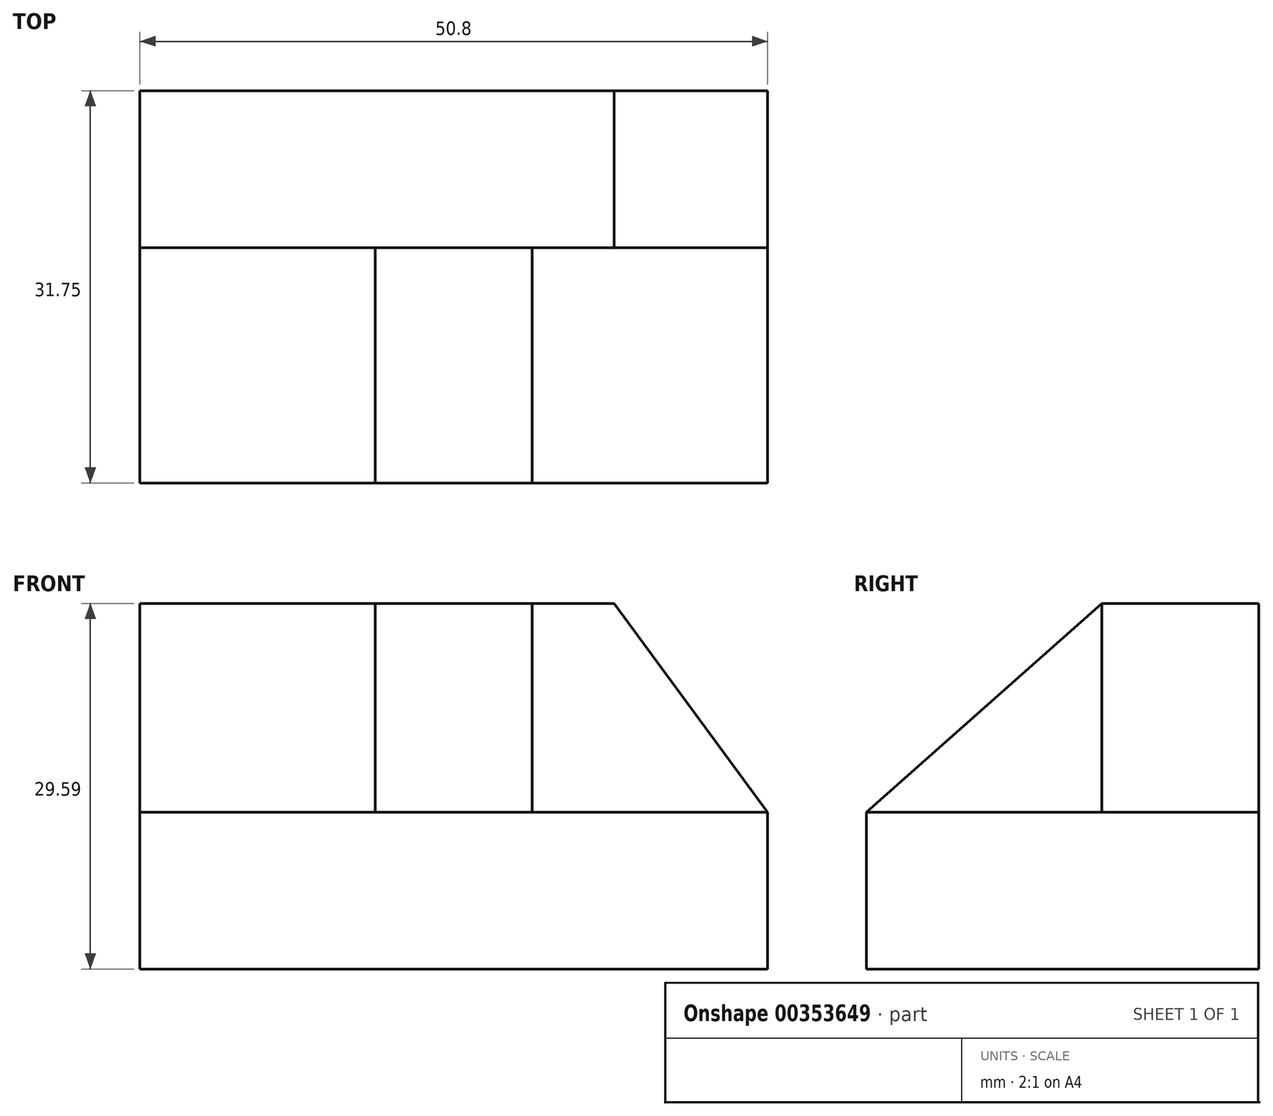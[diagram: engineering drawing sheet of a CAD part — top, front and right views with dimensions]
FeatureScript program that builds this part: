
annotation { "Feature Type Name" : "Feature", "Feature Type Description" : "" }
export const myFeature = defineFeature(function(context is Context, id is Id, definition is map)
    precondition{}
    {
        {
            var Q0;
            Q0=qCreatedBy(makeId("Right.planeOp"),FACE);
            var sketch = newSketch(context, id + "F0", { "sketchPlane" : qUnion([Q0])});
            skLineSegment(sketch, "E0", {"start": v(-31.75, 0) * mm, "end": v(-31.75, 12.7) * mm});
            skLineSegment(sketch, "E1", {"start": v(-31.75, 12.7) * mm, "end": v(-12.7, 12.7) * mm});
            skLineSegment(sketch, "E2", {"start": v(-12.7, 12.7) * mm, "end": v(-12.7, 29.59) * mm});
            skLineSegment(sketch, "E3", {"start": v(-12.7, 29.59) * mm, "end": v(0, 29.59) * mm});
            skLineSegment(sketch, "E4", {"start": v(0, 29.59) * mm, "end": v(0, 0) * mm});
            skLineSegment(sketch, "E5", {"start": v(-31.75, 0) * mm, "end": v(0, 0) * mm});
            skSolve(sketch);
        }
        {
            var Q0;
            Q0 = qSketchRegion(id + "F0", true);
            extrude(context, id + "F1", {"entities" : qUnion([Q0]), "depth" : 50.8 * mm});
        }
        {
            var Q0;
            Q0=makeQuery(id+"F1.opExtrude","SWEPT_FACE",FACE,{"disambiguationData":[OSD([sQuery(id+"F0.wireOp",EDGE,"E2")])]});
            var sketch = newSketch(context, id + "F2", { "sketchPlane" : qUnion([Q0])});
            skLineSegment(sketch, "E6", {"start": v(50.8, 12.7) * mm, "end": v(38.37, 29.59) * mm});
            skLineSegment(sketch, "E7", {"start": v(38.37, 29.59) * mm, "end": v(50.8, 29.59) * mm});
            skLineSegment(sketch, "E8", {"start": v(50.8, 29.59) * mm, "end": v(50.8, 12.7) * mm});
            skSolve(sketch);
        }
        {
            var Q0;
            Q0 = qSketchRegion(id + "F2", true);
            extrude(context, id + "F3", {"entities" : qUnion([Q0]), "operationType" : NewBodyOperationType.REMOVE, "oppositeDirection" : true, "depth" : 25.4 * mm});
        }
        {
            var Q0;
            Q0=makeQuery(id+"F1.opExtrude","SWEPT_FACE",FACE,{"disambiguationData":[OSD([sQuery(id+"F0.wireOp",EDGE,"E1")])]});
            var sketch = newSketch(context, id + "F4", { "sketchPlane" : qUnion([Q0])});
            skLineSegment(sketch, "E9", {"start": v(19.05, -12.7) * mm, "end": v(19.05, -31.75) * mm});
            skLineSegment(sketch, "E10", {"start": v(19.05, -31.75) * mm, "end": v(31.75, -31.75) * mm});
            skLineSegment(sketch, "E11", {"start": v(31.75, -31.75) * mm, "end": v(31.75, -12.7) * mm});
            skLineSegment(sketch, "E12", {"start": v(31.75, -12.7) * mm, "end": v(19.05, -12.7) * mm});
            skSolve(sketch);
        }
        {
            var Q0;
            Q0=makeQuery(id+"F4.imprint","IMPRINT",FACE,{"disambiguationData":[TD([[makeQuery(id+"F4.imprint","IMPRINT",EDGE,{"derivedFrom":sQuery(id+"F4.wireOp",EDGE,"E9")}),1.0]])]});
            extrude(context, id + "F5", {"entities" : qUnion([Q0]), "operationType" : NewBodyOperationType.ADD, "depth" : 17.02 * mm});
        }
        {
            var Q0;
            Q0=makeQuery(id+"F5.opExtrude","SWEPT_FACE",FACE,{"disambiguationData":[OSD([sQuery(id+"F4.wireOp",EDGE,"E11")])]});
            var sketch = newSketch(context, id + "F6", { "sketchPlane" : qUnion([Q0])});
            skLineSegment(sketch, "E13", {"start": v(-31.75, 12.7) * mm, "end": v(-12.7, 29.59) * mm});
            skLineSegment(sketch, "E14", {"start": v(-31.75, 12.7) * mm, "end": v(-31.75, 29.72) * mm});
            skLineSegment(sketch, "E15", {"start": v(-31.75, 29.72) * mm, "end": v(-12.7, 29.72) * mm});
            skSolve(sketch);
        }
        {
            var Q0;
            Q0 = qSketchRegion(id + "F6", true);
            var Q1;
            Q1=makeQuery(id+"F6.imprint","IMPRINT",FACE,{"disambiguationData":[TD([[makeQuery(id+"F6.imprint","IMPRINT",EDGE,{"derivedFrom":sQuery(id+"F6.wireOp",EDGE,"E13")}),1.0]])]});
            extrude(context, id + "F7", {"entities" : qUnion([Q0, Q1]), "operationType" : NewBodyOperationType.REMOVE, "oppositeDirection" : true, "depth" : 25.4 * mm});
        }
    });
